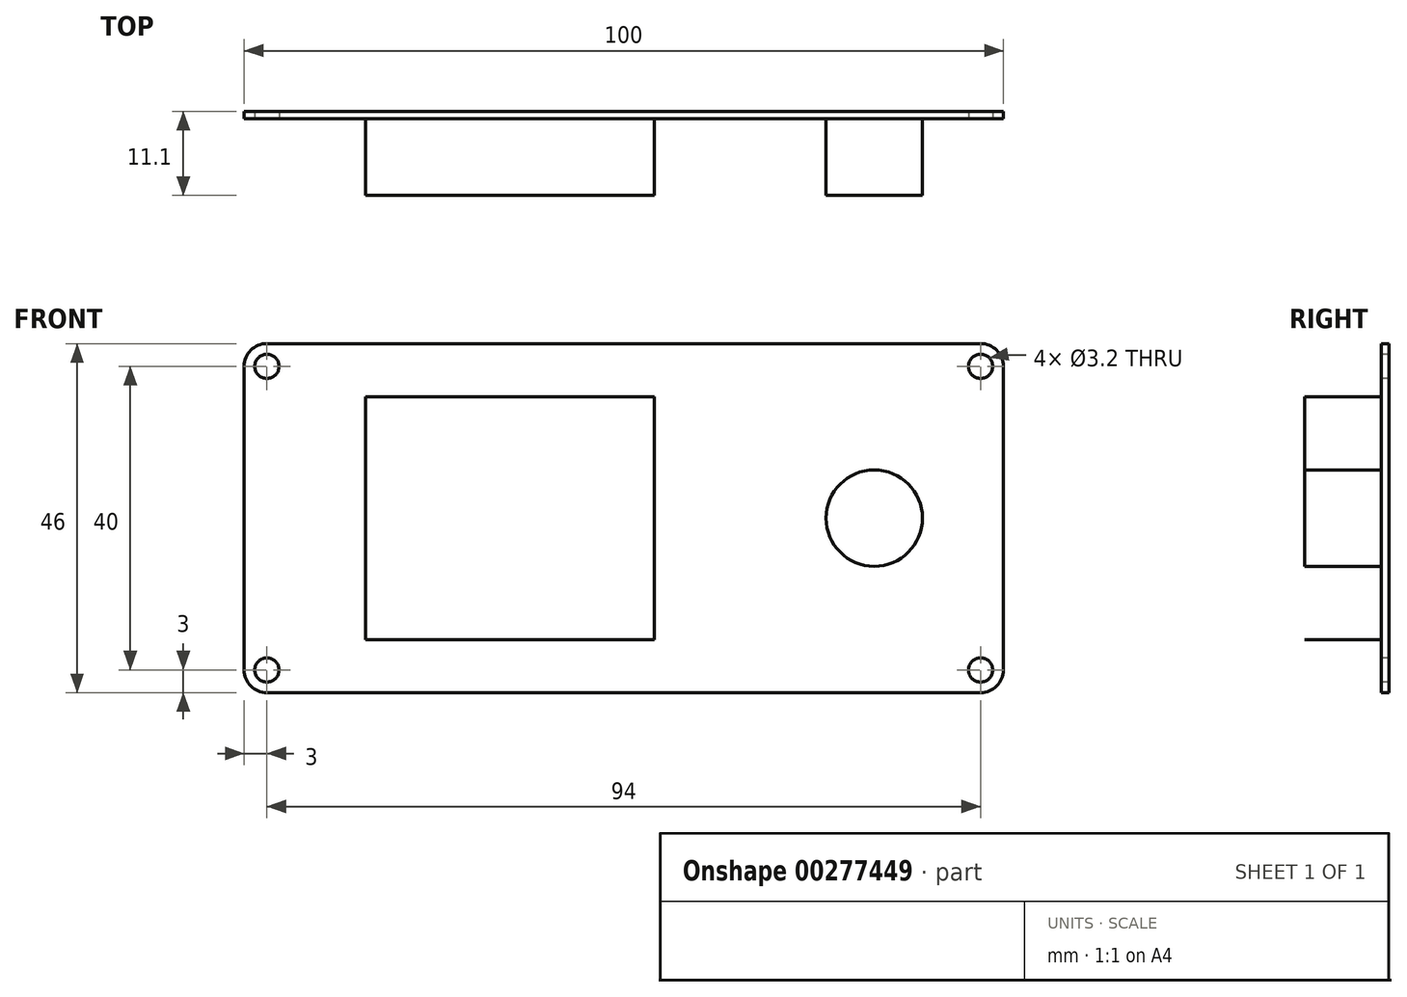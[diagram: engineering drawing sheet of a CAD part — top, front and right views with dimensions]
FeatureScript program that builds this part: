
annotation { "Feature Type Name" : "Feature", "Feature Type Description" : "" }
export const myFeature = defineFeature(function(context is Context, id is Id, definition is map)
    precondition{}
    {
        {
            var Q0;
            Q0=qCreatedBy(makeId("Front.planeOp"),FACE);
            var sketch = newSketch(context, id + "F0", { "sketchPlane" : qUnion([Q0])});
            skLineSegment(sketch, "E0.bottom", {"start": v(19, 16) * mm, "end": v(-19, 16) * mm});
            skLineSegment(sketch, "E0.top", {"start": v(19, -16) * mm, "end": v(-19, -16) * mm});
            skLineSegment(sketch, "E0.left", {"start": v(19, 16) * mm, "end": v(19, -16) * mm});
            skLineSegment(sketch, "E0.right", {"start": v(-19, 16) * mm, "end": v(-19, -16) * mm});
            skPoint(sketch, "E0.middle", {"position": v(0, 0) * mm});
            skCircle(sketch, "E1", {"center": v(48, 0) * mm, "radius": 6.35 * mm});
            skLineSegment(sketch, "E2.top", {"start": v(-32, -23) * mm, "end": v(62, -23) * mm});
            skLineSegment(sketch, "E3", {"start": v(-35, 20) * mm, "end": v(-35, -20) * mm});
            skLineSegment(sketch, "E4", {"start": v(65, 20) * mm, "end": v(65, -20) * mm});
            skLineSegment(sketch, "E5", {"start": v(0, 0) * mm, "end": v(-24.18, 0) * mm, "construction": true});
            skPoint(sketch, "E5.endSnap0", {"position": v(-19, 0) * mm});
            skCircle(sketch, "E6", {"center": v(-32, -20) * mm, "radius": 1.6 * mm});
            skLineSegment(sketch, "E7", {"start": v(-32, 23) * mm, "end": v(62, 23) * mm});
            skCircle(sketch, "E8.MirrorC", {"center": v(-32, 20) * mm, "radius": 1.6 * mm});
            skCircle(sketch, "E9", {"center": v(62, -20) * mm, "radius": 1.6 * mm});
            skPoint(sketch, "E10.visualSharp", {"position": v(65, -23) * mm});
            skArc(sketch, "E10.filletArc", {"start": v(62, -23) * mm, "mid": v(64.12, -22.12) * mm, "end": v(65, -20) * mm});
            skPoint(sketch, "E11.visualSharp", {"position": v(65, 23) * mm});
            skArc(sketch, "E11.filletArc", {"start": v(65, 20) * mm, "mid": v(64.12, 22.12) * mm, "end": v(62, 23) * mm});
            skPoint(sketch, "E12.visualSharp", {"position": v(-35, 23) * mm});
            skArc(sketch, "E12.filletArc", {"start": v(-32, 23) * mm, "mid": v(-34.12, 22.12) * mm, "end": v(-35, 20) * mm});
            skPoint(sketch, "E13.visualSharp", {"position": v(-35, -23) * mm});
            skArc(sketch, "E13.filletArc", {"start": v(-35, -20) * mm, "mid": v(-34.12, -22.12) * mm, "end": v(-32, -23) * mm});
            skCircle(sketch, "E14.MirrorC", {"center": v(62, 20) * mm, "radius": 1.6 * mm});
            skSolve(sketch);
        }
        {
            var Q0;
            Q0=makeQuery(id+"F0.imprint","IMPRINT",FACE,{"disambiguationData":[TD([[makeQuery(id+"F0.imprint","IMPRINT",EDGE,{"derivedFrom":sQuery(id+"F0.wireOp",EDGE,"E0.bottom")}),1.0]])]});
            extrude(context, id + "F1", {"entities" : qUnion([Q0]), "depth" : 10.1 * mm});
        }
        {
            var Q0;
            Q0=makeQuery(id+"F0.imprint","IMPRINT",FACE,{"disambiguationData":[TD([[makeQuery(id+"F0.imprint","IMPRINT",EDGE,{"derivedFrom":sQuery(id+"F0.wireOp",EDGE,"E0.bottom")}),-1.0]])]});
            var Q1;
            Q1=makeQuery(id+"F0.imprint","IMPRINT",FACE,{"disambiguationData":[TD([[makeQuery(id+"F0.imprint","IMPRINT",EDGE,{"derivedFrom":sQuery(id+"F0.wireOp",EDGE,"E0.bottom")}),1.0]])]});
            var Q2;
            Q2=makeQuery(id+"F0.imprint","IMPRINT",FACE,{"disambiguationData":[TD([[makeQuery(id+"F0.imprint","IMPRINT",EDGE,{"derivedFrom":sQuery(id+"F0.wireOp",EDGE,"E1")}),1.0]])]});
            extrude(context, id + "F2", {"entities" : qUnion([Q0, Q1, Q2]), "operationType" : NewBodyOperationType.ADD, "oppositeDirection" : true, "depth" : 1 * mm});
        }
        {
            var Q0;
            Q0=makeQuery(id+"F0.imprint","IMPRINT",FACE,{"disambiguationData":[TD([[makeQuery(id+"F0.imprint","IMPRINT",EDGE,{"derivedFrom":sQuery(id+"F0.wireOp",EDGE,"E1")}),1.0]])]});
            var Q1;
            Q1=makeQuery(id+"F1.opExtrude","CAP_FACE",FACE,{"disambiguationData":[OSD([sQuery(id+"F0.wireOp",EDGE,"E0.bottom"),sQuery(id+"F0.wireOp",EDGE,"E0.top"),sQuery(id+"F0.wireOp",EDGE,"E0.left"),sQuery(id+"F0.wireOp",EDGE,"E0.right")])],"isStart":false});
            extrude(context, id + "F3", {"entities" : qUnion([Q0]), "operationType" : NewBodyOperationType.ADD, "endBound" : BoundingType.UP_TO_SURFACE, "endBoundEntityFace" : qUnion([Q1]), "depth" : 25 * mm});
        }
    });
